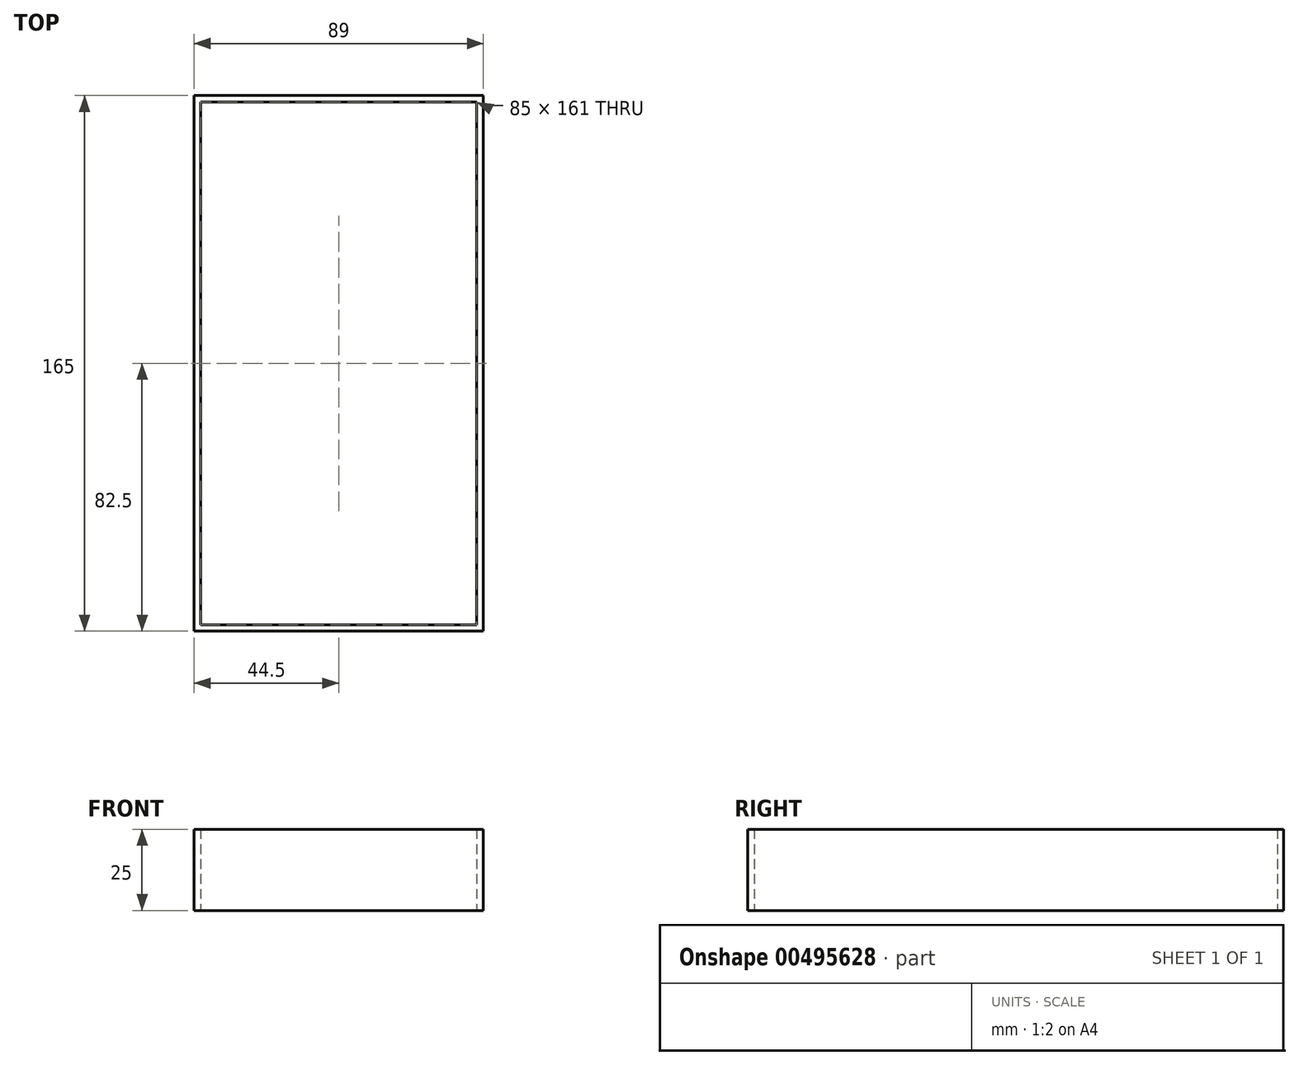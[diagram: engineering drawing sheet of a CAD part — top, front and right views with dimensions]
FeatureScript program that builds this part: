
annotation { "Feature Type Name" : "Feature", "Feature Type Description" : "" }
export const myFeature = defineFeature(function(context is Context, id is Id, definition is map)
    precondition{}
    {
        {
            var Q0;
            Q0=qCreatedBy(makeId("Top.planeOp"),FACE);
            var sketch = newSketch(context, id + "F0", { "sketchPlane" : qUnion([Q0])});
            skLineSegment(sketch, "E0.bottom", {"start": v(0, 0) * mm, "end": v(89, 0) * mm});
            skLineSegment(sketch, "E0.top", {"start": v(0, 165) * mm, "end": v(89, 165) * mm});
            skLineSegment(sketch, "E0.left", {"start": v(0, 0) * mm, "end": v(0, 165) * mm});
            skLineSegment(sketch, "E0.right", {"start": v(89, 0) * mm, "end": v(89, 165) * mm});
            skLineSegment(sketch, "E1.bottom", {"start": v(2, 2) * mm, "end": v(87, 2) * mm});
            skLineSegment(sketch, "E1.top", {"start": v(2, 163) * mm, "end": v(87, 163) * mm});
            skLineSegment(sketch, "E1.left", {"start": v(2, 2) * mm, "end": v(2, 163) * mm});
            skLineSegment(sketch, "E1.right", {"start": v(87, 2) * mm, "end": v(87, 163) * mm});
            skSolve(sketch);
        }
        {
            var Q0;
            Q0=makeQuery(id+"F0.imprint","IMPRINT",FACE,{"disambiguationData":[TD([[makeQuery(id+"F0.imprint","IMPRINT",EDGE,{"derivedFrom":sQuery(id+"F0.wireOp",EDGE,"E0.bottom")}),1.0]])]});
            extrude(context, id + "F1", {"entities" : qUnion([Q0]), "depth" : 25 * mm});
        }
    });
